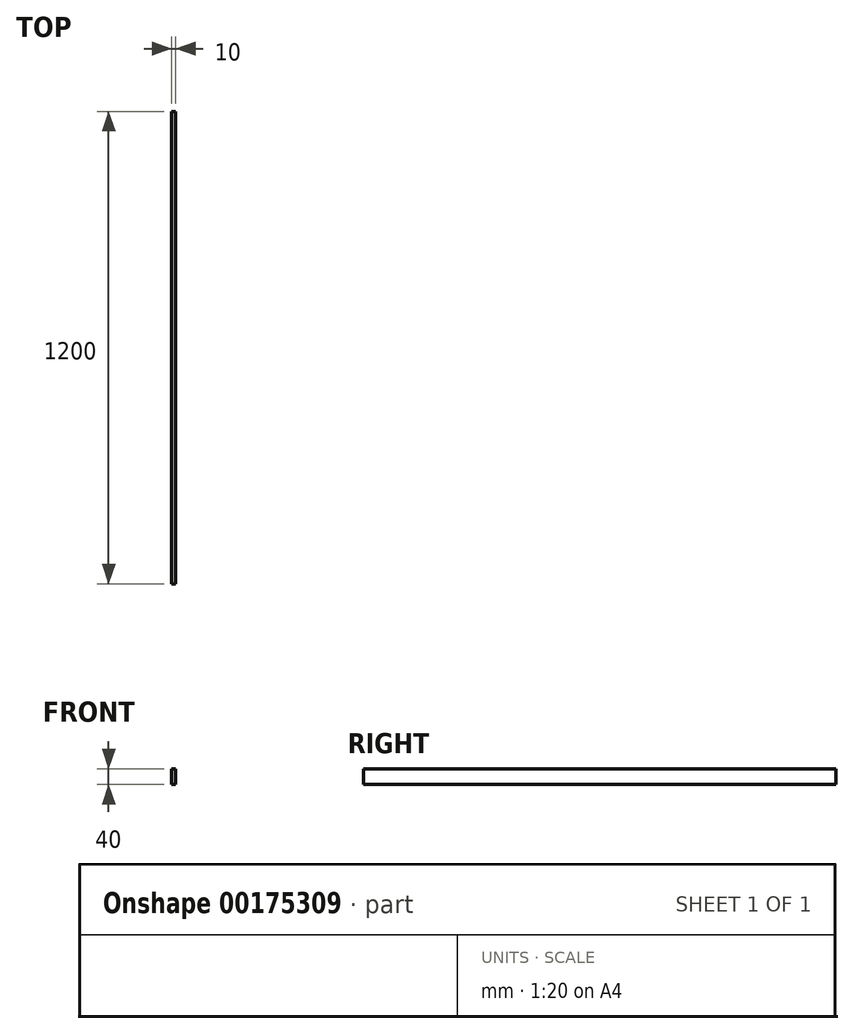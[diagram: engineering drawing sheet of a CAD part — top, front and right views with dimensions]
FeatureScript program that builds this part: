
annotation { "Feature Type Name" : "Feature", "Feature Type Description" : "" }
export const myFeature = defineFeature(function(context is Context, id is Id, definition is map)
    precondition{}
    {
        {
            var Q0;
            Q0=qCreatedBy(makeId("Right.planeOp"),FACE);
            var sketch = newSketch(context, id + "F0", { "sketchPlane" : qUnion([Q0])});
            skLineSegment(sketch, "E0", {"start": v(-600.7, -144.58) * mm, "end": v(599.3, -144.58) * mm});
            skLineSegment(sketch, "E1", {"start": v(-600.7, -144.58) * mm, "end": v(-600.7, -184.58) * mm});
            skLineSegment(sketch, "E2", {"start": v(-600.7, -184.58) * mm, "end": v(599.3, -184.58) * mm});
            skLineSegment(sketch, "E3", {"start": v(599.3, -144.58) * mm, "end": v(599.3, -184.58) * mm});
            skSolve(sketch);
        }
        {
            var Q0;
            Q0 = qSketchRegion(id + "F0", true);
            extrude(context, id + "F1", {"entities" : qUnion([Q0]), "depth" : 10 * mm});
        }
    });
